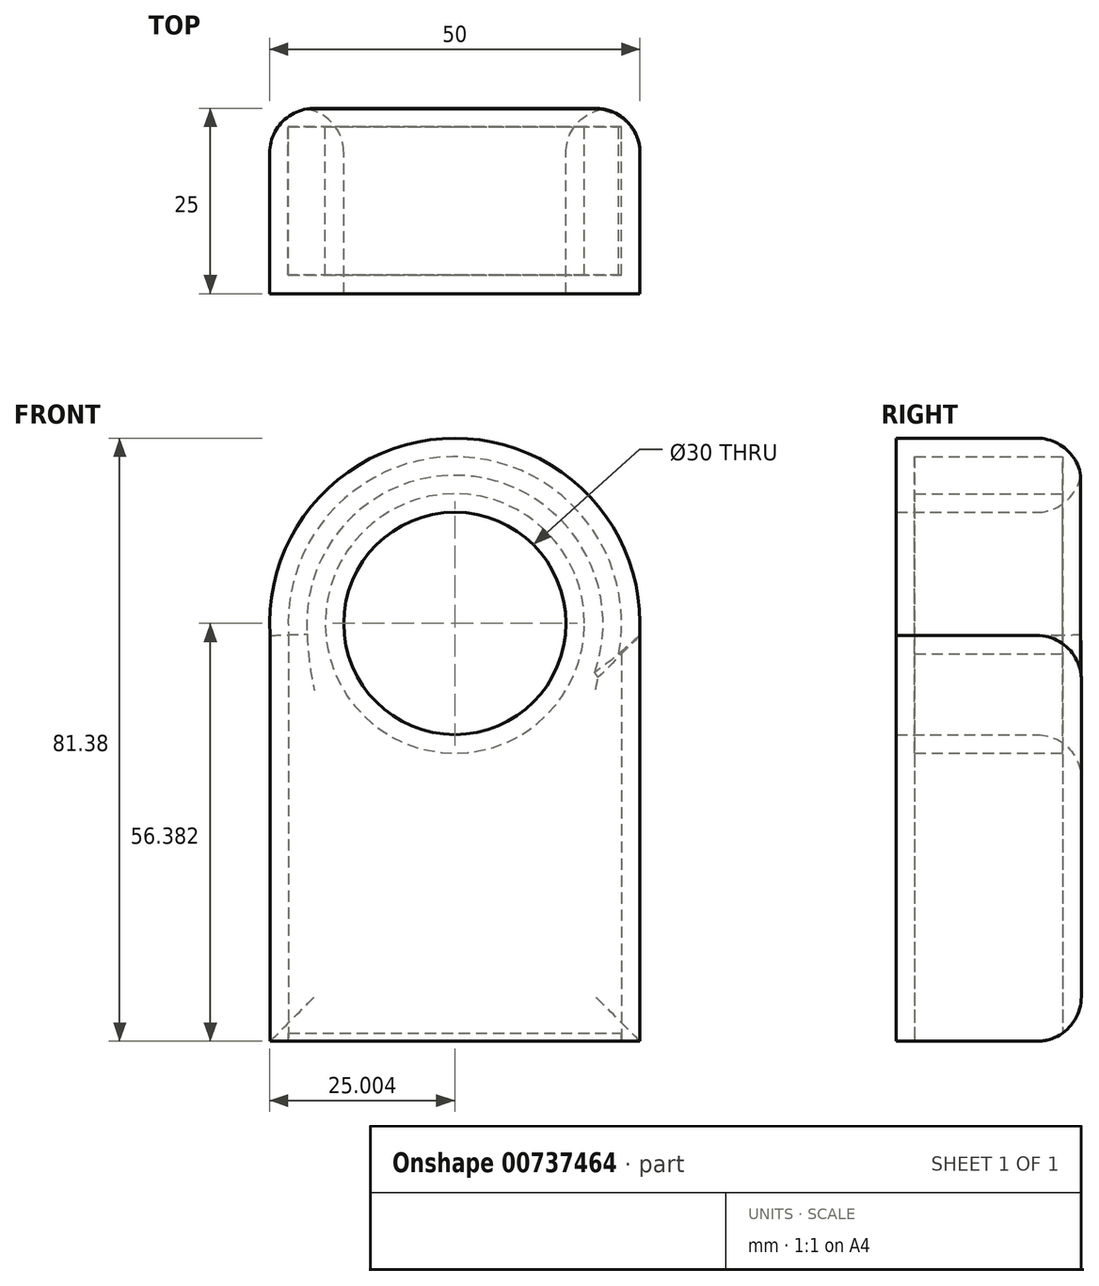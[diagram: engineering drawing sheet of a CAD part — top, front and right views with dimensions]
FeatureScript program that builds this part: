
annotation { "Feature Type Name" : "Feature", "Feature Type Description" : "" }
export const myFeature = defineFeature(function(context is Context, id is Id, definition is map)
    precondition{}
    {
        {
            var Q0;
            Q0=qCreatedBy(makeId("Front.planeOp"),FACE);
            var sketch = newSketch(context, id + "F0", { "sketchPlane" : qUnion([Q0])});
            skCircle(sketch, "E0", {"center": v(-31.13, 20.1) * mm, "radius": 25 * mm});
            skCircle(sketch, "E1", {"center": v(-31.13, 20.1) * mm, "radius": 15 * mm});
            skLineSegment(sketch, "E2.bottom", {"start": v(-56.07, 18.49) * mm, "end": v(-6.13, 18.49) * mm});
            skLineSegment(sketch, "E2.top", {"start": v(-56.07, -36.28) * mm, "end": v(-6.13, -36.28) * mm});
            skLineSegment(sketch, "E2.left", {"start": v(-56.07, 18.49) * mm, "end": v(-56.07, -36.28) * mm});
            skLineSegment(sketch, "E2.right", {"start": v(-6.13, 18.49) * mm, "end": v(-6.13, -36.28) * mm});
            skSolve(sketch);
        }
        {
            var Q0;
            Q0=makeQuery(id+"F0.imprint","IMPRINT",FACE,{"disambiguationData":[TD([[makeQuery(id+"F0.imprint","IMPRINT",EDGE,{"derivedFrom":sQuery(id+"F0.wireOp",EDGE,"E2.top")}),1.0]])]});
            var Q1;
            {var subQ0=sQuery(id+"F0.wireOp",EDGE,"E2.bottom");var subQ4=sQuery(id+"F0.wireOp",EDGE,"E1");var subQ5=makeQuery(id+"F0.imprint","INTERSECT",VERTEX,{"disambiguationData":[OD(0.0)],"derivedFrom":[subQ4,subQ0]});Q1=makeQuery(id+"F0.imprint","IMPRINT",FACE,{"disambiguationData":[TD([[makeQuery(id+"F0.imprint","IMPRINT",EDGE,{"disambiguationData":[TD([[subQ5,-1.0]])],"derivedFrom":subQ4}),-1.0]])]});}
            var Q2;
            {var subQ0=sQuery(id+"F0.wireOp",EDGE,"E2.bottom");var subQ4=sQuery(id+"F0.wireOp",EDGE,"E1");var subQ6=makeQuery(id+"F0.imprint","INTERSECT",VERTEX,{"disambiguationData":[OD(0.0)],"derivedFrom":[subQ4,subQ0]});Q2=makeQuery(id+"F0.imprint","IMPRINT",FACE,{"disambiguationData":[TD([[makeQuery(id+"F0.imprint","IMPRINT",EDGE,{"disambiguationData":[TD([[subQ6,1.0]])],"derivedFrom":subQ4}),-1.0]])]});}
            extrude(context, id + "F1", {"entities" : qUnion([Q0, Q1, Q2]), "depth" : 25 * mm, "offsetDistance" : 25 * mm});
        }
        {
            var Q0;
            Q0=makeQuery(id+"F1.opExtrude","SWEPT_FACE",FACE,{"disambiguationData":[OSD([sQuery(id+"F0.wireOp",EDGE,"E2.top")])]});
            shell(context, id + "F2", {"entities" : qUnion([Q0]), "thickness" : 2.5 * mm});
        }
        {
            var Q0;
            Q0=makeQuery(id+"F1.opExtrude","CAP_EDGE",EDGE,{"disambiguationData":[OSD([sQuery(id+"F0.wireOp",EDGE,"E2.right")])],"isStart":true});
            var Q1;
            Q1=makeQuery(id+"F1.opExtrude","CAP_FACE",FACE,{"disambiguationData":[OSD([sQuery(id+"F0.wireOp",EDGE,"E0"),sQuery(id+"F0.wireOp",EDGE,"E1"),sQuery(id+"F0.wireOp",EDGE,"E2.bottom"),sQuery(id+"F0.wireOp",EDGE,"E2.top"),sQuery(id+"F0.wireOp",EDGE,"E2.left"),sQuery(id+"F0.wireOp",EDGE,"E2.right")])],"isStart":true});
            fillet(context, id + "F3", {"entities" : qUnion([Q0, Q1]), "radius" : 6 * mm, "tangentPropagation" : true, "allowEdgeOverflow" : false});
        }
    });
